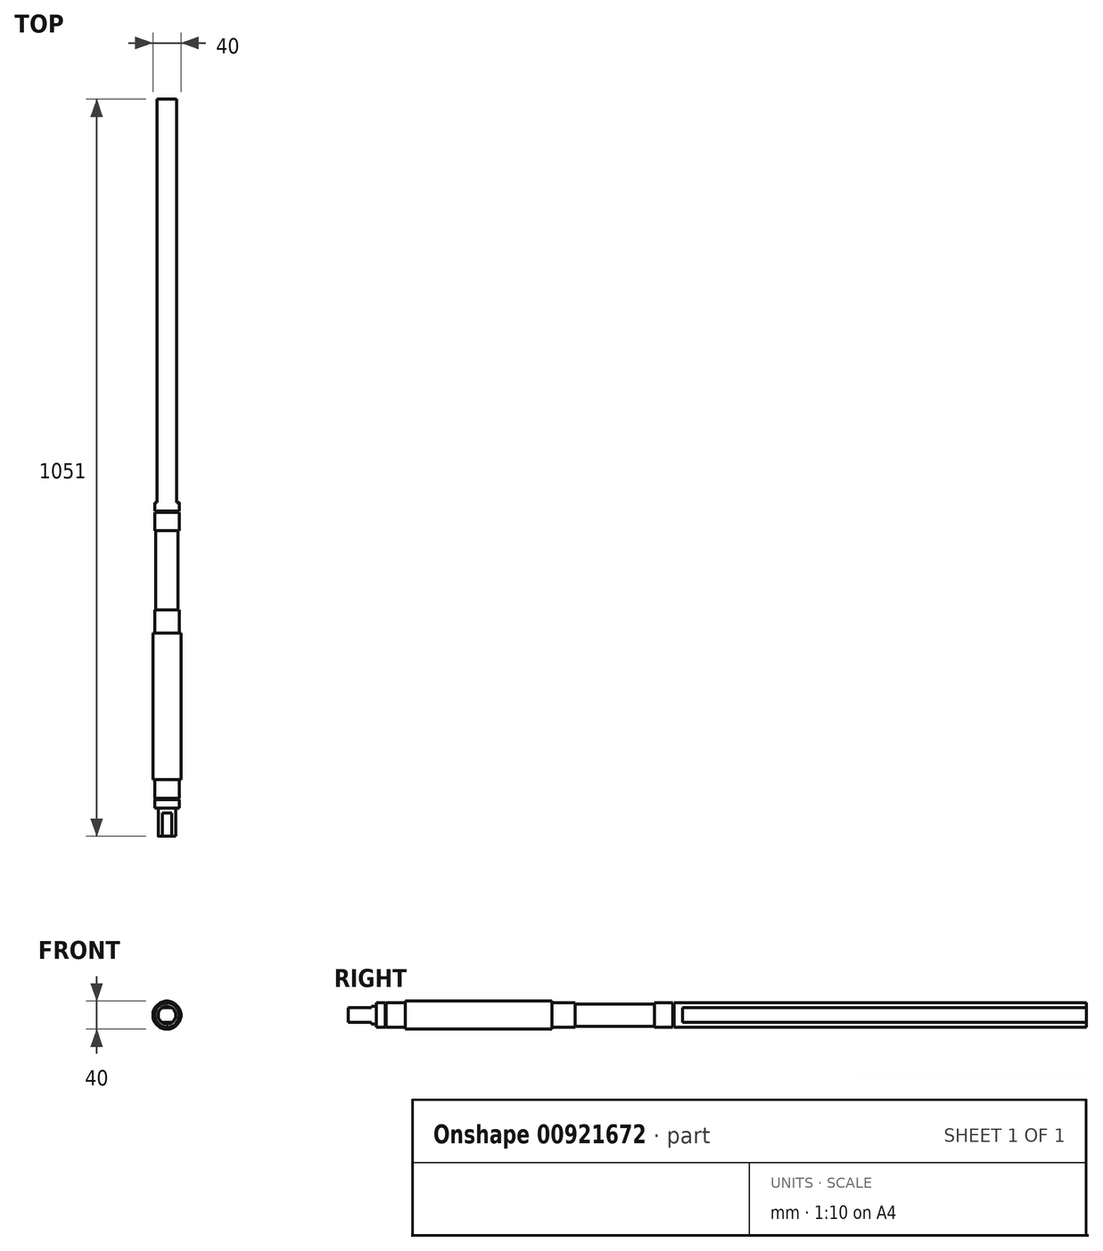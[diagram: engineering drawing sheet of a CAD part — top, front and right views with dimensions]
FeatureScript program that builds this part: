
annotation { "Feature Type Name" : "Feature", "Feature Type Description" : "" }
export const myFeature = defineFeature(function(context is Context, id is Id, definition is map)
    precondition{}
    {
        {
            var Q0;
            Q0=qCreatedBy(makeId("Right.planeOp"),FACE);
            var sketch = newSketch(context, id + "F0", { "sketchPlane" : qUnion([Q0])});
            skLineSegment(sketch, "E0", {"start": v(-44.82, 0) * mm, "end": v(475.4, 0) * mm, "construction": true});
            skLineSegment(sketch, "E1", {"start": v(-21.88, 17.5) * mm, "end": v(-9.48, 17.5) * mm});
            skLineSegment(sketch, "E2", {"start": v(-9.48, 17.5) * mm, "end": v(-9.48, 16.5) * mm});
            skLineSegment(sketch, "E3", {"start": v(-9.48, 16.5) * mm, "end": v(-7.88, 16.5) * mm});
            skLineSegment(sketch, "E4", {"start": v(-7.88, 16.5) * mm, "end": v(-7.88, 17.5) * mm});
            skLineSegment(sketch, "E5", {"start": v(-7.88, 17.5) * mm, "end": v(19.12, 17.5) * mm});
            skLineSegment(sketch, "E6", {"start": v(19.12, 17.5) * mm, "end": v(19.12, 0) * mm});
            skLineSegment(sketch, "E7", {"start": v(19.12, 0) * mm, "end": v(-21.88, 0) * mm});
            skLineSegment(sketch, "E8", {"start": v(-61.88, 12.5) * mm, "end": v(-61.88, 0) * mm});
            skLineSegment(sketch, "E9", {"start": v(-61.88, 0) * mm, "end": v(-21.88, 0) * mm});
            skLineSegment(sketch, "E10", {"start": v(-21.88, 17.5) * mm, "end": v(-21.88, 12.5) * mm});
            skLineSegment(sketch, "E11", {"start": v(-61.88, 12.5) * mm, "end": v(-21.88, 12.5) * mm});
            skLineSegment(sketch, "E12", {"start": v(19.12, 17.5) * mm, "end": v(19.12, 20) * mm});
            skLineSegment(sketch, "E13", {"start": v(19.12, 20) * mm, "end": v(228.12, 20) * mm});
            skLineSegment(sketch, "E14", {"start": v(228.12, 17.5) * mm, "end": v(261.12, 17.5) * mm});
            skLineSegment(sketch, "E15", {"start": v(261.12, 16) * mm, "end": v(374.12, 16) * mm});
            skLineSegment(sketch, "E16", {"start": v(374.12, 16) * mm, "end": v(374.12, 17.5) * mm});
            skLineSegment(sketch, "E17", {"start": v(374.12, 17.5) * mm, "end": v(400.12, 17.5) * mm});
            skLineSegment(sketch, "E18", {"start": v(400.12, 17.5) * mm, "end": v(400.12, 13.73) * mm});
            skLineSegment(sketch, "E19", {"start": v(400.12, 13.73) * mm, "end": v(401.72, 13.73) * mm});
            skLineSegment(sketch, "E20", {"start": v(401.72, 13.73) * mm, "end": v(401.72, 17.5) * mm});
            skLineSegment(sketch, "E21", {"start": v(401.72, 17.5) * mm, "end": v(414.12, 17.5) * mm});
            skLineSegment(sketch, "E22", {"start": v(414.12, 17.5) * mm, "end": v(414.12, 0) * mm});
            skLineSegment(sketch, "E23", {"start": v(19.12, 0) * mm, "end": v(414.12, 0) * mm});
            skLineSegment(sketch, "E24", {"start": v(228.12, 20) * mm, "end": v(228.12, 17.5) * mm});
            skLineSegment(sketch, "E25", {"start": v(261.12, 17.5) * mm, "end": v(261.12, 16) * mm});
            skLineSegment(sketch, "E26", {"start": v(414.12, 17.5) * mm, "end": v(989.12, 17.5) * mm});
            skLineSegment(sketch, "E27", {"start": v(989.12, 17.5) * mm, "end": v(989.12, 0) * mm});
            skLineSegment(sketch, "E28", {"start": v(414.12, 0) * mm, "end": v(989.12, 0) * mm});
            skSolve(sketch);
        }
        {
            var Q0;
            Q0=makeQuery(id+"F0.imprint","IMPRINT",FACE,{"disambiguationData":[TD([[makeQuery(id+"F0.imprint","IMPRINT",EDGE,{"derivedFrom":sQuery(id+"F0.wireOp",EDGE,"E1")}),-1.0]])]});
            var Q1;
            Q1=sQuery(id+"F0.wireOp",EDGE,"E0");
            revolve(context, id + "F1", {"surfaceOperationType" : NewSurfaceOperationType.NEW, "entities" : qUnion([Q0]), "axis" : qUnion([Q1]), "revolveType" : RevolveType.FULL});
        }
        {
            var Q0;
            Q0=makeQuery(id+"F1.opRevolve","SWEPT_FACE",FACE,{"disambiguationData":[OSD([sQuery(id+"F0.wireOp",EDGE,"E8")])]});
            var sketch = newSketch(context, id + "F2", { "sketchPlane" : qUnion([Q0])});
            skLineSegment(sketch, "E29", {"start": v(-21.76, 0) * mm, "end": v(27.37, 0) * mm, "construction": true});
            skLineSegment(sketch, "E30", {"start": v(-6.78, 10.5) * mm, "end": v(6.78, 10.5) * mm});
            skLineSegment(sketch, "E31", {"start": v(-6.78, -10.5) * mm, "end": v(6.78, -10.5) * mm});
            skArc(sketch, "E32", {"start": v(-6.78, 10.5) * mm, "mid": v(0, 12.5) * mm, "end": v(6.78, 10.5) * mm});
            skArc(sketch, "E33", {"start": v(-6.78, -10.5) * mm, "mid": v(0, -12.5) * mm, "end": v(6.78, -10.5) * mm});
            skSolve(sketch);
        }
        {
            var Q0;
            Q0=makeQuery(id+"F2.imprint","IMPRINT",FACE,{"disambiguationData":[TD([[makeQuery(id+"F2.imprint","IMPRINT",EDGE,{"derivedFrom":sQuery(id+"F2.wireOp",EDGE,"E30")}),1.0]])]});
            var Q1;
            Q1=makeQuery(id+"F2.imprint","IMPRINT",FACE,{"disambiguationData":[TD([[makeQuery(id+"F2.imprint","IMPRINT",EDGE,{"derivedFrom":sQuery(id+"F2.wireOp",EDGE,"E31")}),-1.0]])]});
            extrude(context, id + "F3", {"entities" : qUnion([Q0, Q1]), "operationType" : NewBodyOperationType.REMOVE, "oppositeDirection" : true, "depth" : 33 * mm, "offsetDistance" : 25 * mm});
        }
        {
            var Q0;
            Q0=makeQuery(id+"F0.imprint","IMPRINT",FACE,{"disambiguationData":[TD([[makeQuery(id+"F0.imprint","IMPRINT",EDGE,{"derivedFrom":sQuery(id+"F0.wireOp",EDGE,"E6")}),1.0]])]});
            var Q1;
            Q1=sQuery(id+"F0.wireOp",EDGE,"E23");
            revolve(context, id + "F4", {"operationType" : NewBodyOperationType.ADD, "surfaceOperationType" : NewSurfaceOperationType.NEW, "entities" : qUnion([Q0]), "axis" : qUnion([Q1]), "revolveType" : RevolveType.FULL});
        }
        {
            var Q0;
            Q0=makeQuery(id+"F0.imprint","IMPRINT",FACE,{"disambiguationData":[TD([[makeQuery(id+"F0.imprint","IMPRINT",EDGE,{"derivedFrom":sQuery(id+"F0.wireOp",EDGE,"E22")}),1.0]])]});
            var Q1;
            Q1=sQuery(id+"F0.wireOp",EDGE,"E28");
            revolve(context, id + "F5", {"operationType" : NewBodyOperationType.ADD, "surfaceOperationType" : NewSurfaceOperationType.NEW, "entities" : qUnion([Q0]), "axis" : qUnion([Q1]), "revolveType" : RevolveType.FULL});
        }
        {
            var Q0;
            Q0=makeQuery(id+"F5.opRevolve","SWEPT_FACE",FACE,{"disambiguationData":[OSD([sQuery(id+"F0.wireOp",EDGE,"E27")])]});
            var sketch = newSketch(context, id + "F6", { "sketchPlane" : qUnion([Q0])});
            skPoint(sketch, "E34", {"position": v(0, 0) * mm});
            skLineSegment(sketch, "E35", {"start": v(-30.38, 0) * mm, "end": v(58.38, 0) * mm, "construction": true});
            skLineSegment(sketch, "E36", {"start": v(0, 31.4) * mm, "end": v(0, -45.9) * mm, "construction": true});
            skLineSegment(sketch, "E37", {"start": v(-14, 10.5) * mm, "end": v(-14, -10.5) * mm});
            skLineSegment(sketch, "E38", {"start": v(14, 10.5) * mm, "end": v(14, -10.5) * mm});
            skPoint(sketch, "E38.endSnap0", {"position": v(14, 0) * mm});
            skArc(sketch, "E39", {"start": v(-14, 10.5) * mm, "mid": v(-17.5, 0) * mm, "end": v(-14, -10.5) * mm});
            skArc(sketch, "E40", {"start": v(14, 10.5) * mm, "mid": v(17.5, 0) * mm, "end": v(14, -10.5) * mm});
            skSolve(sketch);
        }
        {
            var Q0;
            Q0=makeQuery(id+"F6.imprint","IMPRINT",FACE,{"disambiguationData":[TD([[makeQuery(id+"F6.imprint","IMPRINT",EDGE,{"derivedFrom":sQuery(id+"F6.wireOp",EDGE,"E38")}),1.0]])]});
            var Q1;
            Q1=makeQuery(id+"F6.imprint","IMPRINT",FACE,{"disambiguationData":[TD([[makeQuery(id+"F6.imprint","IMPRINT",EDGE,{"derivedFrom":sQuery(id+"F6.wireOp",EDGE,"E37")}),-1.0]])]});
            extrude(context, id + "F7", {"entities" : qUnion([Q0, Q1]), "operationType" : NewBodyOperationType.REMOVE, "oppositeDirection" : true, "depth" : 575 * mm, "offsetDistance" : 25 * mm});
        }
    });
